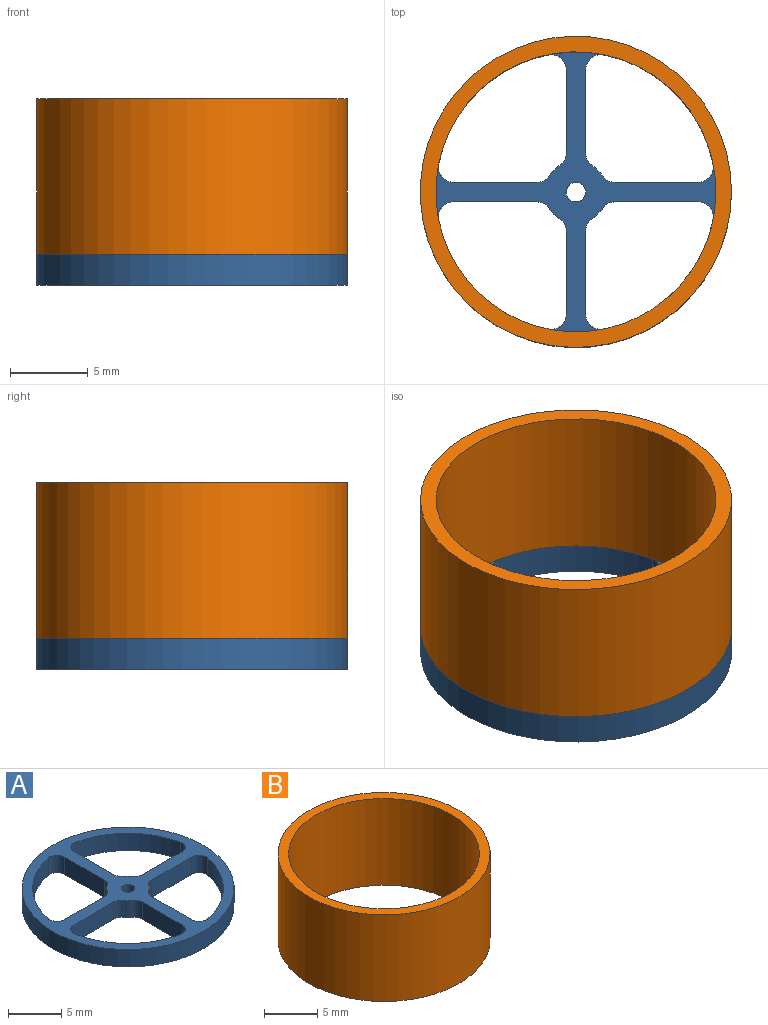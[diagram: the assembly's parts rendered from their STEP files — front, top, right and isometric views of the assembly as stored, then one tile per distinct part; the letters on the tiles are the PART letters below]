
ASSEMBLY  parts=2 mates=1
PART A: 36 faces, bbox 20x20x2 mm
  f0: cylinder r=9mm len=6.98mm, axis (0,0,-1), area 20.9mm2, adj f1,f28,f34,f35
  f1: cylinder r=1mm len=2mm, axis (0,0,-1), area 3.6mm2, adj f0,f2,f34,f35
  f2: plane 5.31x2mm, normal (-1,0,0), area 10.6mm2, adj f1,f3,f34,f35
  f3: cylinder r=1mm len=2mm, axis (0,0,-1), area 2mm2, adj f2,f4,f34,f35
  f4: cylinder r=2mm len=2mm, axis (0,0,-1), area 1.7mm2, adj f3,f5,f34,f35
  f5: cylinder r=1mm len=2mm, axis (0,0,-1), area 2mm2, adj f4,f6,f34,f35
  f6: plane 5.31x2mm, normal (0,1,0), area 10.6mm2, adj f5,f28,f34,f35
  f7: plane 5.31x2mm, normal (0,-1,0), area 10.6mm2, adj f8,f29,f34,f35
  f8: cylinder r=1mm len=2mm, axis (0,0,-1), area 2mm2, adj f7,f9,f34,f35
  f9: cylinder r=2mm len=2mm, axis (0,0,-1), area 1.7mm2, adj f8,f10,f34,f35
  f10: cylinder r=1mm len=2mm, axis (0,0,-1), area 2mm2, adj f9,f11,f34,f35
  f11: plane 5.31x2mm, normal (-1,0,0), area 10.6mm2, adj f10,f12,f34,f35
  f12: cylinder r=1mm len=2mm, axis (0,0,-1), area 3.6mm2, adj f11,f13,f34,f35
  f13: cylinder r=9mm len=6.98mm, axis (0,0,-1), area 20.9mm2, adj f12,f29,f34,f35
  f14: cylinder r=1mm len=2mm, axis (0,0,-1), area 2mm2, adj f15,f30,f34,f35
  f15: cylinder r=2mm len=2mm, axis (0,0,-1), area 1.7mm2, adj f14,f16,f34,f35
  f16: cylinder r=1mm len=2mm, axis (0,0,-1), area 2mm2, adj f15,f17,f34,f35
  f17: plane 5.31x2mm, normal (1,0,0), area 10.6mm2, adj f16,f18,f34,f35
  f18: cylinder r=1mm len=2mm, axis (0,0,-1), area 3.6mm2, adj f17,f19,f34,f35
  f19: cylinder r=9mm len=6.98mm, axis (0,0,-1), area 20.9mm2, adj f18,f20,f34,f35
  f20: cylinder r=1mm len=2mm, axis (0,0,-1), area 3.6mm2, adj f19,f30,f34,f35
  f21: cylinder r=1mm len=2mm, axis (0,0,-1), area 3.6mm2, adj f22,f31,f34,f35
  f22: plane 5.31x2mm, normal (1,0,0), area 10.6mm2, adj f21,f23,f34,f35
  f23: cylinder r=1mm len=2mm, axis (0,0,-1), area 2mm2, adj f22,f24,f34,f35
  f24: cylinder r=2mm len=2mm, axis (0,0,-1), area 1.7mm2, adj f23,f25,f34,f35
  f25: cylinder r=1mm len=2mm, axis (0,0,-1), area 2mm2, adj f24,f26,f34,f35
  f26: plane 5.31x2mm, normal (0,-1,0), area 10.6mm2, adj f25,f27,f34,f35
  f27: cylinder r=1mm len=2mm, axis (0,0,-1), area 3.6mm2, adj f26,f31,f34,f35
  f28: cylinder r=1mm len=2mm, axis (0,0,-1), area 3.6mm2, adj f0,f6,f34,f35
  f29: cylinder r=1mm len=2mm, axis (0,0,-1), area 3.6mm2, adj f7,f13,f34,f35
  f30: plane 5.31x2mm, normal (0,1,0), area 10.6mm2, adj f14,f20,f34,f35
  f31: cylinder r=9mm len=6.98mm, axis (0,0,-1), area 20.9mm2, adj f21,f27,f34,f35
  f32: cylinder r=0.62mm len=2mm, axis (0,0,-1), area 7.9mm2, adj f34,f35
  f33: cylinder r=10mm len=20mm, axis (0,0,-1), area 125.7mm2, adj f34,f35
  f34: plane 20x20mm, normal (0,0,1), area 109.1mm2, adj f0,f1,f2,f3,f4,f5,f6,f7
  f35: plane 20x20mm, normal (0,0,-1), area 109.1mm2, adj f0,f1,f2,f3,f4,f5,f6,f7
PART B: 4 faces, bbox 20x20x10 mm
  f0: cylinder r=9mm len=18mm, axis (0,0,-1), area 565.5mm2, adj f2,f3
  f1: cylinder r=10mm len=20mm, axis (0,0,-1), area 628.3mm2, adj f2,f3
  f2: plane 20x20mm, normal (0,0,1), area 59.7mm2, adj f0,f1
  f3: plane 20x20mm, normal (0,0,-1), area 59.7mm2, adj f0,f1
PLACE A at identity fixed
PLACE B t=(0,0,2)mm
MATE fastened A.f0 <-> B.f0  axis (0,0,1) through (0,0,2)mm
